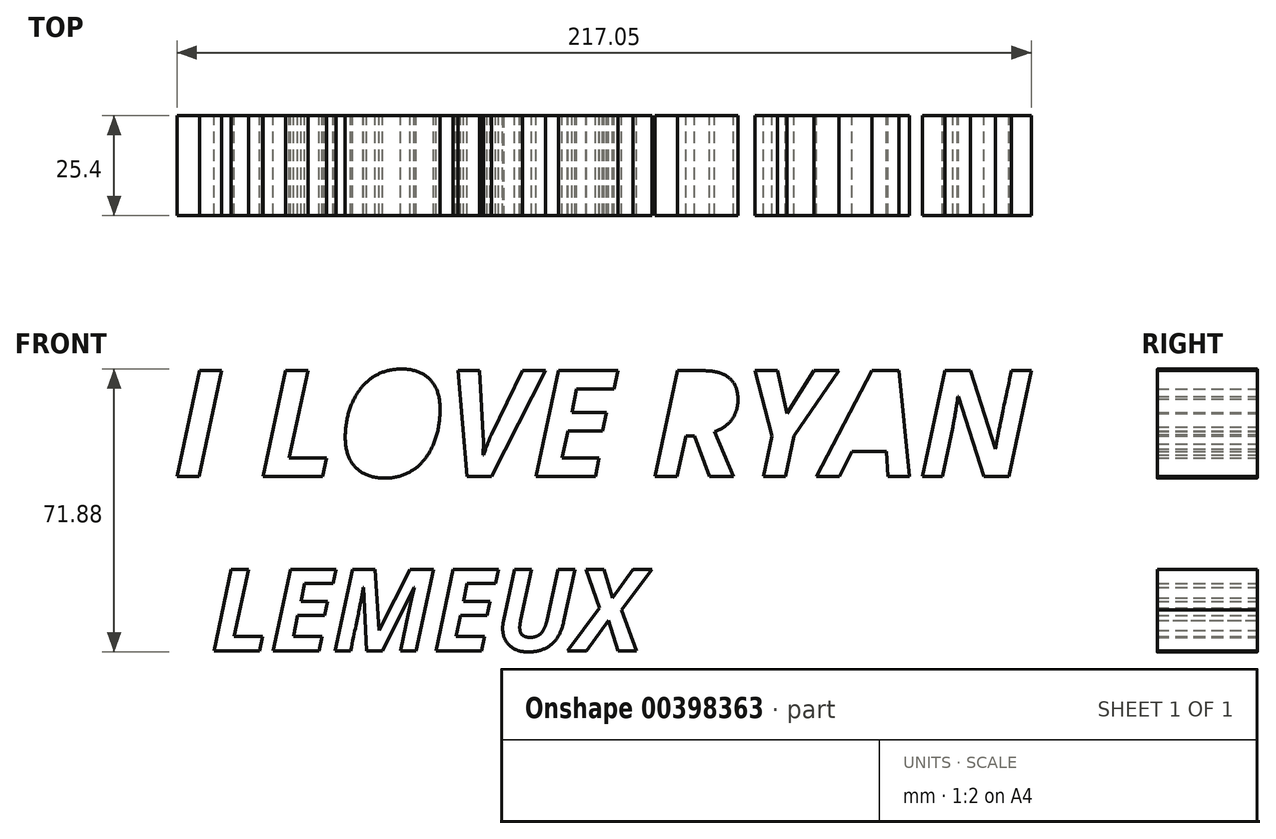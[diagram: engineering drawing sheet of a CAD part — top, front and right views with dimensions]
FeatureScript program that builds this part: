
annotation { "Feature Type Name" : "Feature", "Feature Type Description" : "" }
export const myFeature = defineFeature(function(context is Context, id is Id, definition is map)
    precondition{}
    {
        {
            var Q0;
            Q0=qCreatedBy(makeId("Front.planeOp"),FACE);
            var sketch = newSketch(context, id + "F0", { "sketchPlane" : qUnion([Q0])});
            skText(sketch, "E0", { "text": "I LOVE RYAN", "fontName": "OpenSans-BoldItalic.ttf"});
            skText(sketch, "E1", { "text": "LEMEUX", "fontName": "OpenSans-BoldItalic.ttf"});
            const initialGuessF0  = {"E0": [-0.08822, 0.0386, 1, 0, 0.02715], "E1": [-0.07857, -0.00565, 1, 0, 0.02091]};
            skSetInitialGuess(sketch, initialGuessF0);
            skSolve(sketch);
        }
        {
            var Q0;
            Q0=makeQuery(id+"F0.imprint","IMPRINT",FACE,{"disambiguationData":[TD([[makeQuery(id+"F0.imprint","IMPRINT",EDGE,{"derivedFrom":sQuery(id+"F0.wireOp",EDGE,"E0.sketch_text.stroke-81")}),-1.0]])]});
            var Q1;
            Q1=makeQuery(id+"F0.imprint","IMPRINT",FACE,{"disambiguationData":[TD([[makeQuery(id+"F0.imprint","IMPRINT",EDGE,{"derivedFrom":sQuery(id+"F0.wireOp",EDGE,"E0.sketch_text.stroke-89")}),1.0]])]});
            var Q2;
            Q2=makeQuery(id+"F0.imprint","IMPRINT",FACE,{"disambiguationData":[TD([[makeQuery(id+"F0.imprint","IMPRINT",EDGE,{"derivedFrom":sQuery(id+"F0.wireOp",EDGE,"E0.sketch_text.stroke-53")}),-1.0]])]});
            var Q3;
            Q3=makeQuery(id+"F0.imprint","IMPRINT",FACE,{"disambiguationData":[TD([[makeQuery(id+"F0.imprint","IMPRINT",EDGE,{"derivedFrom":sQuery(id+"F0.wireOp",EDGE,"E0.sketch_text.stroke-20")}),1.0]])]});
            var Q4;
            Q4=makeQuery(id+"F0.imprint","IMPRINT",FACE,{"disambiguationData":[TD([[makeQuery(id+"F0.imprint","IMPRINT",EDGE,{"derivedFrom":sQuery(id+"F0.wireOp",EDGE,"E0.sketch_text.stroke-53")}),1.0]])]});
            var Q5;
            Q5=makeQuery(id+"F0.imprint","IMPRINT",FACE,{"disambiguationData":[TD([[makeQuery(id+"F0.imprint","IMPRINT",EDGE,{"derivedFrom":sQuery(id+"F0.wireOp",EDGE,"E0.sketch_text.stroke-0")}),-1.0]])]});
            var Q6;
            Q6=makeQuery(id+"F0.imprint","IMPRINT",FACE,{"disambiguationData":[TD([[makeQuery(id+"F0.imprint","IMPRINT",EDGE,{"derivedFrom":sQuery(id+"F0.wireOp",EDGE,"E0.sketch_text.stroke-4")}),-1.0]])]});
            var Q7;
            Q7=makeQuery(id+"F0.imprint","IMPRINT",FACE,{"disambiguationData":[TD([[makeQuery(id+"F0.imprint","IMPRINT",EDGE,{"derivedFrom":sQuery(id+"F0.wireOp",EDGE,"E0.sketch_text.stroke-30")}),-1.0]])]});
            var Q8;
            Q8=makeQuery(id+"F0.imprint","IMPRINT",FACE,{"disambiguationData":[TD([[makeQuery(id+"F0.imprint","IMPRINT",EDGE,{"derivedFrom":sQuery(id+"F0.wireOp",EDGE,"E0.sketch_text.stroke-41")}),-1.0]])]});
            var Q9;
            Q9=makeQuery(id+"F0.imprint","IMPRINT",FACE,{"disambiguationData":[TD([[makeQuery(id+"F0.imprint","IMPRINT",EDGE,{"derivedFrom":sQuery(id+"F0.wireOp",EDGE,"E0.sketch_text.stroke-72")}),-1.0]])]});
            var Q10;
            Q10=makeQuery(id+"F0.imprint","IMPRINT",FACE,{"disambiguationData":[TD([[makeQuery(id+"F0.imprint","IMPRINT",EDGE,{"derivedFrom":sQuery(id+"F0.wireOp",EDGE,"E0.sketch_text.stroke-95")}),-1.0]])]});
            var Q11;
            Q11=makeQuery(id+"F0.imprint","IMPRINT",FACE,{"disambiguationData":[TD([[makeQuery(id+"F0.imprint","IMPRINT",EDGE,{"derivedFrom":sQuery(id+"F0.wireOp",EDGE,"E1.sketch_text.stroke-0")}),-1.0]])]});
            var Q12;
            Q12=makeQuery(id+"F0.imprint","IMPRINT",FACE,{"disambiguationData":[TD([[makeQuery(id+"F0.imprint","IMPRINT",EDGE,{"derivedFrom":sQuery(id+"F0.wireOp",EDGE,"E1.sketch_text.stroke-6")}),-1.0]])]});
            var Q13;
            Q13=makeQuery(id+"F0.imprint","IMPRINT",FACE,{"disambiguationData":[TD([[makeQuery(id+"F0.imprint","IMPRINT",EDGE,{"derivedFrom":sQuery(id+"F0.wireOp",EDGE,"E1.sketch_text.stroke-18")}),-1.0]])]});
            var Q14;
            Q14=makeQuery(id+"F0.imprint","IMPRINT",FACE,{"disambiguationData":[TD([[makeQuery(id+"F0.imprint","IMPRINT",EDGE,{"derivedFrom":sQuery(id+"F0.wireOp",EDGE,"E1.sketch_text.stroke-36")}),-1.0]])]});
            var Q15;
            Q15=makeQuery(id+"F0.imprint","IMPRINT",FACE,{"disambiguationData":[TD([[makeQuery(id+"F0.imprint","IMPRINT",EDGE,{"derivedFrom":sQuery(id+"F0.wireOp",EDGE,"E1.sketch_text.stroke-48")}),-1.0]])]});
            var Q16;
            Q16=makeQuery(id+"F0.imprint","IMPRINT",FACE,{"disambiguationData":[TD([[makeQuery(id+"F0.imprint","IMPRINT",EDGE,{"derivedFrom":sQuery(id+"F0.wireOp",EDGE,"E1.sketch_text.stroke-63")}),-1.0]])]});
            var Q17;
            Q17=makeQuery(id+"F0.imprint","IMPRINT",FACE,{"disambiguationData":[TD([[makeQuery(id+"F0.imprint","IMPRINT",EDGE,{"derivedFrom":sQuery(id+"F0.wireOp",EDGE,"E0.sketch_text.stroke-10")}),-1.0]])]});
            extrude(context, id + "F1", {"entities" : qUnion([Q0, Q1, Q2, Q3, Q4, Q5, Q6, Q7, Q8, Q9, Q10, Q11, Q12, Q13, Q14, Q15, Q16, Q17]), "depth" : 25.4 * mm});
        }
    });
